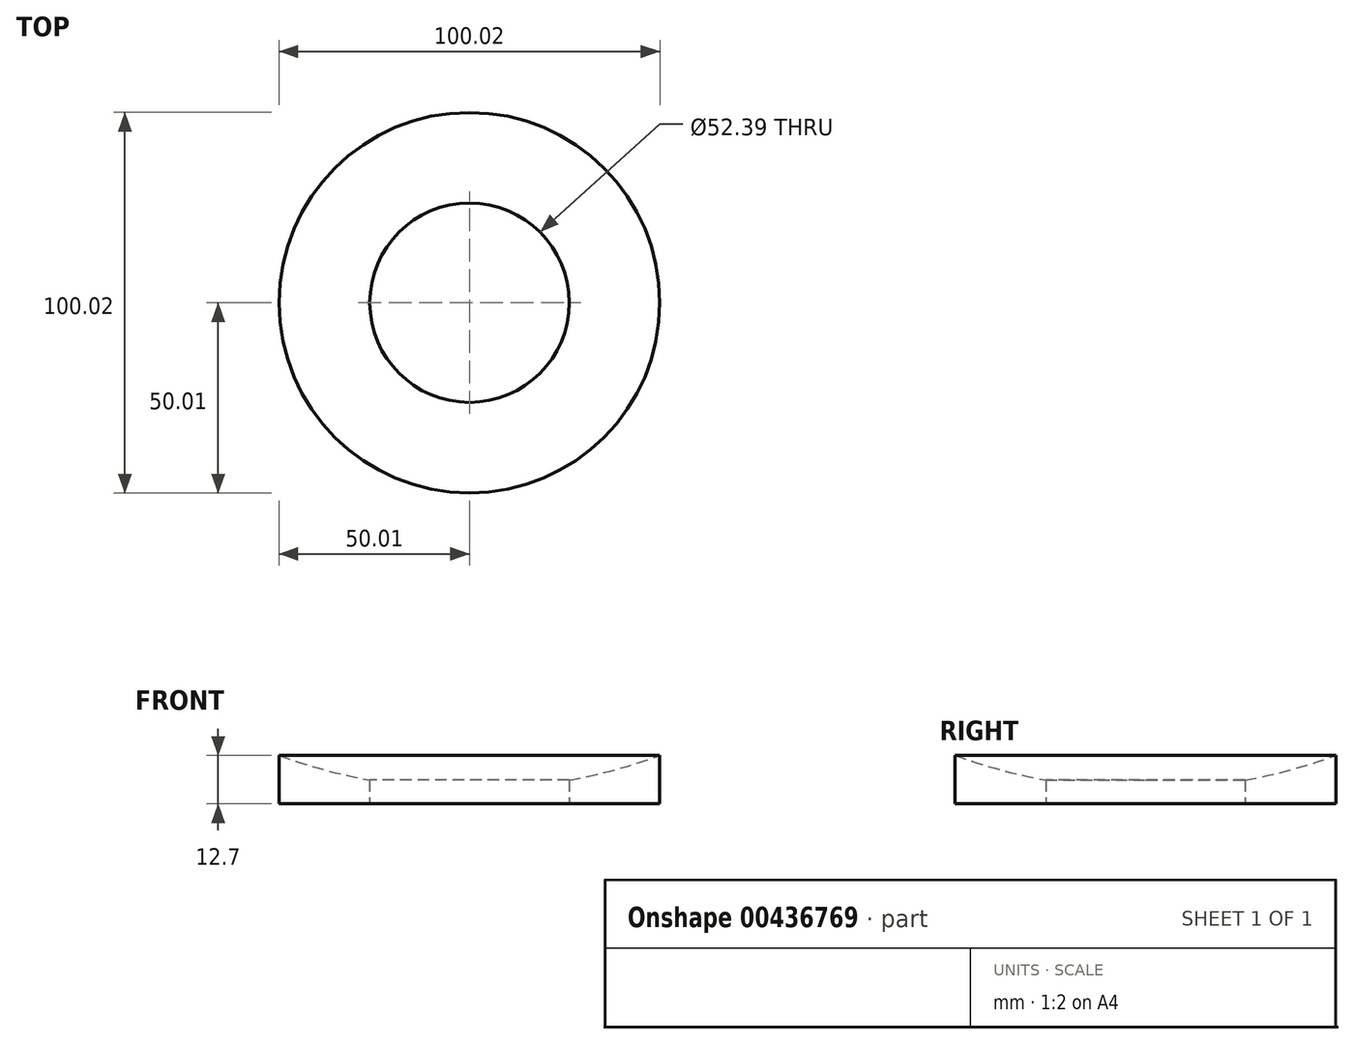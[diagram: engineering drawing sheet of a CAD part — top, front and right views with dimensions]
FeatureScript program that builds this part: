
annotation { "Feature Type Name" : "Feature", "Feature Type Description" : "" }
export const myFeature = defineFeature(function(context is Context, id is Id, definition is map)
    precondition{}
    {
        {
            var Q0;
            Q0=qCreatedBy(makeId("Top.planeOp"),FACE);
            var sketch = newSketch(context, id + "F0", { "sketchPlane" : qUnion([Q0])});
            skCircle(sketch, "E0", {"center": v(0, 0) * mm, "radius": 50 * mm});
            skCircle(sketch, "E1", {"center": v(0, 0) * mm, "radius": 26.2 * mm});
            skSolve(sketch);
        }
        {
            var Q0;
            Q0=makeQuery(id+"F0.imprint","IMPRINT",FACE,{"disambiguationData":[TD([[makeQuery(id+"F0.imprint","IMPRINT",EDGE,{"derivedFrom":sQuery(id+"F0.wireOp",EDGE,"E0")}),1.0]])]});
            extrude(context, id + "F1", {"entities" : qUnion([Q0]), "depth" : 12.7 * mm});
        }
        {
            var Q0;
            Q0=qCreatedBy(makeId("Front.planeOp"),FACE);
            var sketch = newSketch(context, id + "F2", { "sketchPlane" : qUnion([Q0])});
            skArc(sketch, "E2", {"start": v(0, 3.87) * mm, "mid": v(146.05, 149.92) * mm, "end": v(0, 295.97) * mm});
            skLineSegment(sketch, "E3", {"start": v(0, 3.87) * mm, "end": v(0, 295.97) * mm});
            skLineSegment(sketch, "E4.0", {"start": v(-50, 12.7) * mm, "end": v(50, 12.7) * mm});
            skSolve(sketch);
        }
        {
            var Q0;
            Q0=makeQuery(id+"F2.imprint","IMPRINT",FACE,{"disambiguationData":[TD([[makeQuery(id+"F2.imprint","IMPRINT",EDGE,{"derivedFrom":sQuery(id+"F2.wireOp",EDGE,"E2")}),1.0]])]});
            var Q1;
            Q1=sQuery(id+"F2.wireOp",EDGE,"E3");
            revolve(context, id + "F3", {"operationType" : NewBodyOperationType.REMOVE, "entities" : qUnion([Q0]), "axis" : qUnion([Q1]), "revolveType" : RevolveType.FULL, "oppositeDirection" : true});
        }
    });
